# Revit family: Legrand-Ups-Keor_T-10_120kVA
name_source: partatom
category: Installations électriques
revit_build: Autodesk Revit 2018 (Build: 20170223_1515(x64)
units: mm (PartAtom-declared; Revit-internal decimal feet)

## family parameters
Basée sur le plan de construction = Non
Conserver l'orientation des annotations = Non
Cote de connecteur circulaire = Utiliser le diamètre
Couper avec des vides une fois chargée = Non
Numéro OmniClass = 23.80.10.17.34
Partagée = Non
Point de calcul de pièce = Non
Titre OmniClass = Static Uninterruptible Power Supplies
Toujours verticalement = Oui
Type d'élément = Normal

## types (65) — shared parameters
Back Clearance = 250 mm  [stored 0.82021 ft]
Conductors = Cables
Connection constraint = Back and bottom
Connection constraint (signal) = Back and bottom
Fabricant = LEGRAND
Frequency of use = 50 Hz or 60 Hz selectable
Front Clearance = 700 mm  [stored 2.29659 ft]
General Conditions of Use = https://export.legrand.com
Humidity = 20-95% not condensing
Input / Output phase configuration = 3ph+N+PE
Installation type = On the floor
Max sound pressure level = < 55 dB at 1m
Modèle = KEOR T
Operating altitude = up to 1000 m altitude without derating
Operating temperature = from 0°C to +40°C
Output Voltage = 380,400,415 Vac
Output power factor = 0.9
URL = https://ups.legrand.com
Visibilità aree d'installazione = Oui

## per-type parameters (varying)
| type | Active power of use | Cabinet Depth | Cabinet Height | Cabinet Width | Installation space | Nominal Power | Side Clearance | Weight |
| LG-310200 | 9 kW | 800 mm  [stored 2.62467 ft] | 1345 mm | 400 mm  [stored 1.31234 ft] | 0.43 m³ | 10 kVA | 500 mm  [stored 1.64042 ft] | 118.0 kg |
| LG-310196 | 9 kW | 800 mm  [stored 2.62467 ft] | 1345 mm | 400 mm  [stored 1.31234 ft] | 0.43 m³ | 10 kVA | 500 mm  [stored 1.64042 ft] | 118.0 kg |
| LG-310223 | 9 kW | 800 mm  [stored 2.62467 ft] | 1650 mm  [stored 5.41339 ft] | 400 mm  [stored 1.31234 ft] | 0.43 m³ | 10 kVA | 500 mm  [stored 1.64042 ft] | 158.0 kg |
| LG-310201 | 9 kW | 800 mm  [stored 2.62467 ft] | 1345 mm | 400 mm  [stored 1.31234 ft] | 0.43 m³ | 10 kVA | 500 mm  [stored 1.64042 ft] | 253.0 kg |
| LG-310202 | 9 kW | 800 mm  [stored 2.62467 ft] | 1345 mm | 400 mm  [stored 1.31234 ft] | 0.43 m³ | 10 kVA | 500 mm  [stored 1.64042 ft] | 283.0 kg |
| LG-310203 | 9 kW | 800 mm  [stored 2.62467 ft] | 1650 mm  [stored 5.41339 ft] | 400 mm  [stored 1.31234 ft] | 0.43 m³ | 10 kVA | 500 mm  [stored 1.64042 ft] | 406.0 kg |
| LG-310204 | 14 kW | 800 mm  [stored 2.62467 ft] | 1345 mm | 400 mm  [stored 1.31234 ft] | 0.43 m³ | 15 kVA | 500 mm  [stored 1.64042 ft] | 132.0 kg |
| LG-310197 | 14 kW | 800 mm  [stored 2.62467 ft] | 1345 mm | 400 mm  [stored 1.31234 ft] | 0.43 m³ | 15 kVA | 500 mm  [stored 1.64042 ft] | 132.0 kg |
| LG-310224 | 14 kW | 800 mm  [stored 2.62467 ft] | 1650 mm  [stored 5.41339 ft] | 400 mm  [stored 1.31234 ft] | 0.52 m³ | 15 kVA | 500 mm  [stored 1.64042 ft] | 161.0 kg |
| LG-310205 | 14 kW | 800 mm  [stored 2.62467 ft] | 1345 mm | 400 mm  [stored 1.31234 ft] | 0.43 m³ | 15 kVA | 500 mm  [stored 1.64042 ft] | 267.0 kg |
| LG-310206 | 14 kW | 800 mm  [stored 2.62467 ft] | 1345 mm | 400 mm  [stored 1.31234 ft] | 0.43 m³ | 15 kVA | 500 mm  [stored 1.64042 ft] | 297.0 kg |
| LG-310207 | 14 kW | 800 mm  [stored 2.62467 ft] | 1650 mm  [stored 5.41339 ft] | 400 mm  [stored 1.31234 ft] | 0.52 m³ | 15 kVA | 500 mm  [stored 1.64042 ft] | 420.0 kg |
| LG-310208 | 18 kW | 800 mm  [stored 2.62467 ft] | 1345 mm | 400 mm  [stored 1.31234 ft] | 0.43 m³ | 20 kVA | 500 mm  [stored 1.64042 ft] | 134.0 kg |
| LG-310198 | 18 kW | 800 mm  [stored 2.62467 ft] | 1345 mm | 400 mm  [stored 1.31234 ft] | 0.43 m³ | 20 kVA | 500 mm  [stored 1.64042 ft] | 134.0 kg |
| LG-310225 | 18 kW | 800 mm  [stored 2.62467 ft] | 1650 mm  [stored 5.41339 ft] | 400 mm  [stored 1.31234 ft] | 0.52 m³ | 20 kVA | 500 mm  [stored 1.64042 ft] | 163.0 kg |
| LG-310209 | 18 kW | 800 mm  [stored 2.62467 ft] | 1345 mm | 400 mm  [stored 1.31234 ft] | 0.43 m³ | 20 kVA | 500 mm  [stored 1.64042 ft] | 269.0 kg |
| LG-310210 | 18 kW | 800 mm  [stored 2.62467 ft] | 1345 mm | 400 mm  [stored 1.31234 ft] | 0.43 m³ | 20 kVA | 500 mm  [stored 1.64042 ft] | 299.0 kg |
| LG-310211 | 18 kW | 800 mm  [stored 2.62467 ft] | 1650 mm  [stored 5.41339 ft] | 400 mm  [stored 1.31234 ft] | 0.43 m³ | 20 kVA | 500 mm  [stored 1.64042 ft] | 494.0 kg |
| LG-310212 | 27 kW | 800 mm  [stored 2.62467 ft] | 1345 mm | 400 mm  [stored 1.31234 ft] | 0.43 m³ | 30 kVA | 500 mm  [stored 1.64042 ft] | 140.0 kg |
| LG-310199 | 27 kW | 800 mm  [stored 2.62467 ft] | 1345 mm | 400 mm  [stored 1.31234 ft] | 0.43 m³ | 30 kVA | 500 mm  [stored 1.64042 ft] | 140.0 kg |
| LG-310226 | 27 kW | 800 mm  [stored 2.62467 ft] | 1650 mm  [stored 5.41339 ft] | 400 mm  [stored 1.31234 ft] | 0.52 m³ | 30 kVA | 500 mm  [stored 1.64042 ft] | 180.0 kg |
| LG-310213 | 27 kW | 800 mm  [stored 2.62467 ft] | 1345 mm | 400 mm  [stored 1.31234 ft] | 0.43 m³ | 30 kVA | 500 mm  [stored 1.64042 ft] | 305.0 kg |
| LG-310214 | 27 kW | 800 mm  [stored 2.62467 ft] | 1345 mm | 400 mm  [stored 1.31234 ft] | 0.43 m³ | 30 kVA | 500 mm  [stored 1.64042 ft] | 428.0 kg |
| LG-310215 | 27 kW | 800 mm  [stored 2.62467 ft] | 1345 mm | 400 mm  [stored 1.31234 ft] | 0.43 m³ | 30 kVA | 500 mm  [stored 1.64042 ft] | 488.0 kg |
| LG-310216 | 36 kW | 900 mm  [stored 2.95276 ft] | 1650 mm  [stored 5.41339 ft] | 600 mm | 0.89 m³ | 40 kVA | 700 mm  [stored 2.29659 ft] | 255.0 kg |
| LG-310927 | 36 kW | 900 mm  [stored 2.95276 ft] | 1650 mm  [stored 5.41339 ft] | 600 mm | 0.89 m³ | 40 kVA | 700 mm  [stored 2.29659 ft] | 241.0 kg |
| LG-310217 | 36 kW | 900 mm  [stored 2.95276 ft] | 1650 mm  [stored 5.41339 ft] | 600 mm | 0.89 m³ | 40 kVA | 700 mm  [stored 2.29659 ft] | 539.0 kg |
| LG-310218 | 36 kW | 900 mm  [stored 2.95276 ft] | 1650 mm  [stored 5.41339 ft] | 600 mm | 0.89 m³ | 40 kVA | 700 mm  [stored 2.29659 ft] | 598.0 kg |
| LG-310219 | 36 kW | 900 mm  [stored 2.95276 ft] | 1650 mm  [stored 5.41339 ft] | 600 mm | 0.89 m³ | 40 kVA | 700 mm  [stored 2.29659 ft] | 748.0 kg |
| LG-310220 | 54 kW | 900 mm  [stored 2.95276 ft] | 1650 mm  [stored 5.41339 ft] | 600 mm | 0.89 m³ | 60 kVA | 700 mm  [stored 2.29659 ft] | 277.0 kg |
| LG-310928 | 54 kW | 900 mm  [stored 2.95276 ft] | 1650 mm  [stored 5.41339 ft] | 600 mm | 0.89 m³ | 60 kVA | 700 mm  [stored 2.29659 ft] | 276.0 kg |
| LG-310221 | 54 kW | 900 mm  [stored 2.95276 ft] | 1650 mm  [stored 5.41339 ft] | 600 mm | 0.89 m³ | 60 kVA | 700 mm  [stored 2.29659 ft] | 620.0 kg |
| LG-310222 | 54 kW | 900 mm  [stored 2.95276 ft] | 1650 mm  [stored 5.41339 ft] | 600 mm | 0.89 m³ | 60 kVA | 700 mm  [stored 2.29659 ft] | 770.0 kg |
| LG-310227 | 72 kW | 980 mm  [stored 3.21522 ft] | 1650 mm  [stored 5.41339 ft] | 600 mm | 0.97 m³ | 80 kVA | 500 mm  [stored 1.64042 ft] | 315.0 kg |
| LG-310228 | 90 kW | 980 mm  [stored 3.21522 ft] | 1650 mm  [stored 5.41339 ft] | 600 mm | 0.97 m³ | 100 kVA | 500 mm  [stored 1.64042 ft] | 350.0 kg |
| LG-310229 | 108 kW | 800 mm  [stored 2.62467 ft] | 1650 mm  [stored 5.41339 ft] | 800 mm  [stored 2.62467 ft] | 1 m³ | 120 kVA | 500 mm  [stored 1.64042 ft] | 430.0 kg |
| LG-310230 | 9 kW | 800 mm  [stored 2.62467 ft] | 1345 mm | 400 mm  [stored 1.31234 ft] | 0.43 m³ | 10 kVA | 500 mm  [stored 1.64042 ft] | 240.0 kg |
| LG-310231 | 14 kW | 800 mm  [stored 2.62467 ft] | 1345 mm | 400 mm  [stored 1.31234 ft] | 0.43 m³ | 15 kVA | 500 mm  [stored 1.64042 ft] | 250.0 kg |
| LG-310232 | 18 kW | 800 mm  [stored 2.62467 ft] | 1345 mm | 400 mm  [stored 1.31234 ft] | 0.43 m³ | 20 kVA | 500 mm  [stored 1.64042 ft] | 255.0 kg |
| LG-310233 | 27 kW | 800 mm  [stored 2.62467 ft] | 1345 mm | 400 mm  [stored 1.31234 ft] | 0.43 m³ | 30 kVA | 500 mm  [stored 1.64042 ft] | 285.0 kg |
| LG-310234 | 36 kW | 900 mm  [stored 2.95276 ft] | 1650 mm  [stored 5.41339 ft] | 600 mm | 0.89 m³ | 40 kVA | 700 mm  [stored 2.29659 ft] | 525.0 kg |
| LG-310235 | 54 kW | 900 mm  [stored 2.95276 ft] | 1650 mm  [stored 5.41339 ft] | 600 mm | 0.89 m³ | 60 kVA | 700 mm  [stored 2.29659 ft] | 575.0 kg |
| LG-310236 | 9 kW | 800 mm  [stored 2.62467 ft] | 1345 mm | 400 mm  [stored 1.31234 ft] | 0.43 m³ | 10 kVA | 500 mm  [stored 1.64042 ft] | 118.0 kg |
| LG-310237 | 9 kW | 800 mm  [stored 2.62467 ft] | 1345 mm | 400 mm  [stored 1.31234 ft] | 0.43 m³ | 10 kVA | 500 mm  [stored 1.64042 ft] | 253.0 kg |
| LG-310238 | 9 kW | 800 mm  [stored 2.62467 ft] | 1345 mm | 400 mm  [stored 1.31234 ft] | 0.43 m³ | 10 kVA | 500 mm  [stored 1.64042 ft] | 283.0 kg |
| LG-310239 | 9 kW | 800 mm  [stored 2.62467 ft] | 1650 mm  [stored 5.41339 ft] | 400 mm  [stored 1.31234 ft] | 0.43 m³ | 10 kVA | 500 mm  [stored 1.64042 ft] | 406.0 kg |
| LG-310240 | 14 kW | 800 mm  [stored 2.62467 ft] | 1345 mm | 400 mm  [stored 1.31234 ft] | 0.43 m³ | 15 kVA | 500 mm  [stored 1.64042 ft] | 132.0 kg |
| LG-310241 | 14 kW | 800 mm  [stored 2.62467 ft] | 1345 mm | 400 mm  [stored 1.31234 ft] | 0.43 m³ | 15 kVA | 500 mm  [stored 1.64042 ft] | 267.0 kg |
| LG-310242 | 14 kW | 800 mm  [stored 2.62467 ft] | 1345 mm | 400 mm  [stored 1.31234 ft] | 0.43 m³ | 15 kVA | 500 mm  [stored 1.64042 ft] | 297.0 kg |
| LG-310243 | 14 kW | 800 mm  [stored 2.62467 ft] | 1650 mm  [stored 5.41339 ft] | 400 mm  [stored 1.31234 ft] | 0.52 m³ | 15 kVA | 500 mm  [stored 1.64042 ft] | 420.0 kg |
| LG-310244 | 18 kW | 800 mm  [stored 2.62467 ft] | 1345 mm | 400 mm  [stored 1.31234 ft] | 0.43 m³ | 20 kVA | 500 mm  [stored 1.64042 ft] | 134.0 kg |
| LG-310245 | 18 kW | 800 mm  [stored 2.62467 ft] | 1345 mm | 400 mm  [stored 1.31234 ft] | 0.43 m³ | 20 kVA | 500 mm  [stored 1.64042 ft] | 269.0 kg |
| LG-310246 | 18 kW | 800 mm  [stored 2.62467 ft] | 1345 mm | 400 mm  [stored 1.31234 ft] | 0.43 m³ | 20 kVA | 500 mm  [stored 1.64042 ft] | 299.0 kg |
| LG-310247 | 18 kW | 800 mm  [stored 2.62467 ft] | 1650 mm  [stored 5.41339 ft] | 400 mm  [stored 1.31234 ft] | 0.43 m³ | 20 kVA | 500 mm  [stored 1.64042 ft] | 494.0 kg |
| LG-310248 | 27 kW | 800 mm  [stored 2.62467 ft] | 1345 mm | 400 mm  [stored 1.31234 ft] | 0.43 m³ | 30 kVA | 500 mm  [stored 1.64042 ft] | 140.0 kg |
| LG-310249 | 27 kW | 800 mm  [stored 2.62467 ft] | 1345 mm | 400 mm  [stored 1.31234 ft] | 0.43 m³ | 30 kVA | 500 mm  [stored 1.64042 ft] | 305.0 kg |
| LG-310250 | 27 kW | 800 mm  [stored 2.62467 ft] | 1345 mm | 400 mm  [stored 1.31234 ft] | 0.43 m³ | 30 kVA | 500 mm  [stored 1.64042 ft] | 428.0 kg |
| LG-310251 | 27 kW | 800 mm  [stored 2.62467 ft] | 1345 mm | 400 mm  [stored 1.31234 ft] | 0.43 m³ | 30 kVA | 500 mm  [stored 1.64042 ft] | 488.0 kg |
| LG-310252 | 36 kW | 900 mm  [stored 2.95276 ft] | 1650 mm  [stored 5.41339 ft] | 600 mm | 0.89 m³ | 40 kVA | 700 mm  [stored 2.29659 ft] | 255.0 kg |
| LG-310253 | 36 kW | 900 mm  [stored 2.95276 ft] | 1650 mm  [stored 5.41339 ft] | 600 mm | 0.89 m³ | 40 kVA | 700 mm  [stored 2.29659 ft] | 539.0 kg |
| LG-310254 | 36 kW | 900 mm  [stored 2.95276 ft] | 1650 mm  [stored 5.41339 ft] | 600 mm | 0.89 m³ | 40 kVA | 700 mm  [stored 2.29659 ft] | 598.0 kg |
| LG-310255 | 36 kW | 900 mm  [stored 2.95276 ft] | 1650 mm  [stored 5.41339 ft] | 600 mm | 0.89 m³ | 40 kVA | 700 mm  [stored 2.29659 ft] | 748.0 kg |
| LG-310256 | 54 kW | 900 mm  [stored 2.95276 ft] | 1650 mm  [stored 5.41339 ft] | 600 mm | 0.89 m³ | 60 kVA | 700 mm  [stored 2.29659 ft] | 277.0 kg |
| LG-310257 | 54 kW | 900 mm  [stored 2.95276 ft] | 1650 mm  [stored 5.41339 ft] | 600 mm | 0.89 m³ | 60 kVA | 700 mm  [stored 2.29659 ft] | 620.0 kg |
| LG-310258 | 54 kW | 900 mm  [stored 2.95276 ft] | 1650 mm  [stored 5.41339 ft] | 600 mm | 0.89 m³ | 60 kVA | 700 mm  [stored 2.29659 ft] | 770.0 kg |

note: [stored X ft] marks values corroborated as IEEE doubles in the binary element streams (Revit-internal decimal feet)
